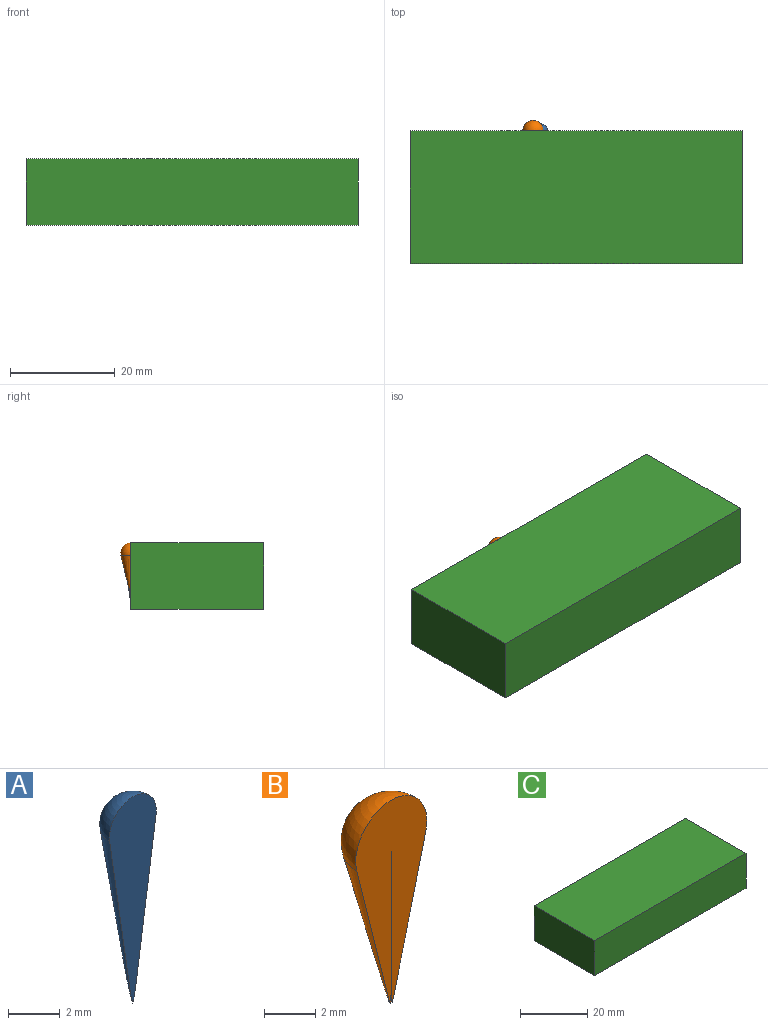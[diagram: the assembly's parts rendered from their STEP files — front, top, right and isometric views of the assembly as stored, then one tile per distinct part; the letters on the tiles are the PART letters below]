
ASSEMBLY  parts=3 mates=2
PART A: 3 faces, bbox 2.6x1.3x9.8 mm
  f0: sphere r=1.28mm, area 5.9mm2, adj f1,f2
  f1: revolved ~8.3x2.54mm, area 17.6mm2, adj f0,f2
  f2: plane 9.78x2.58mm, normal (0,-1,0), area 14.1mm2, adj f0,f1
PART B: 3 faces, bbox 3.9x2.2x10.1 mm
  f0: sphere r=1.96mm, area 15.1mm2, adj f1,f2
  f1: revolved ~7.24x3.81mm, area 23.5mm2, adj f0,f2
  f2: plane 10.07x3.94mm, normal (0,-1,0), area 19.5mm2, adj f0,f1
PART C: 6 faces, bbox 63.5x25.4x12.7 mm
  f0: plane 63.5x12.7mm, normal (0,-1,0), area 806.5mm2, adj f1,f3,f4,f5
  f1: plane 25.4x12.7mm, normal (1,0,0), area 322.6mm2, adj f0,f2,f4,f5
  f2: plane 63.5x12.7mm, normal (0,1,0), area 806.5mm2, adj f1,f3,f4,f5
  f3: plane 25.4x12.7mm, normal (-1,0,0), area 322.6mm2, adj f0,f2,f4,f5
  f4: plane 63.5x25.4mm, normal (0,0,1), area 1612.9mm2, adj f0,f1,f2,f3
  f5: plane 63.5x25.4mm, normal (0,0,-1), area 1612.9mm2, adj f0,f1,f2,f3
PLACE A t=(-45.64,-50.81,17.47)mm
PLACE B t=(-47.11,-50.81,17.89)mm
PLACE C rot(axis=(1,0,0),180deg) t=(-38.92,-63.51,20.31)mm
MATE planar A.f2 <-> C.f0  axis (0,-1,0) through (-45.64,-50.81,15.34)mm
MATE planar C.f0 <-> B.f2  axis (0,1,0) through (-38.92,-50.81,13.96)mm
